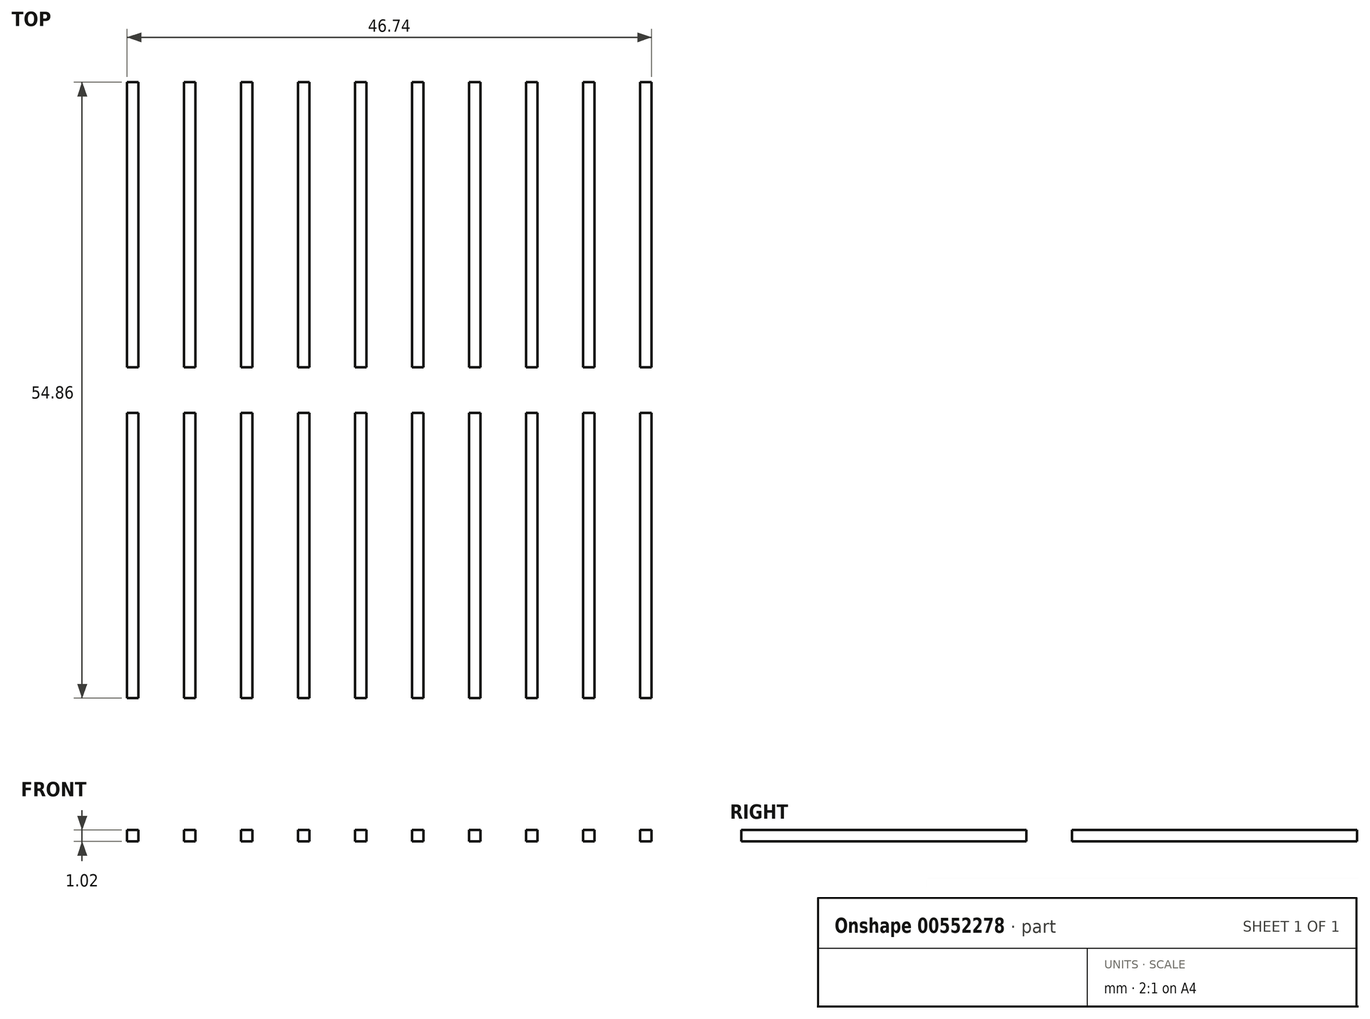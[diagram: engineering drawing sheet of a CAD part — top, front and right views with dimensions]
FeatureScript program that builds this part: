
annotation { "Feature Type Name" : "Feature", "Feature Type Description" : "" }
export const myFeature = defineFeature(function(context is Context, id is Id, definition is map)
    precondition{}
    {
        {
            var Q0;
            Q0=qCreatedBy(makeId("Top.planeOp"),FACE);
            var sketch = newSketch(context, id + "F0", { "sketchPlane" : qUnion([Q0])});
            skLineSegment(sketch, "E0.bottom", {"start": v(0, 0) * mm, "end": v(1.02, 0) * mm});
            skLineSegment(sketch, "E0.top", {"start": v(0, 25.4) * mm, "end": v(1.02, 25.4) * mm});
            skLineSegment(sketch, "E0.left", {"start": v(0, 0) * mm, "end": v(0, 25.4) * mm});
            skLineSegment(sketch, "E0.right", {"start": v(1.02, 0) * mm, "end": v(1.02, 25.4) * mm});
            skLineSegment(sketch, "E1.1.0.0", {"start": v(6.1, 0) * mm, "end": v(6.1, 25.4) * mm});
            skLineSegment(sketch, "E1.1.0.1", {"start": v(5.08, 0) * mm, "end": v(5.08, 25.4) * mm});
            skLineSegment(sketch, "E1.1.0.2", {"start": v(5.08, 25.4) * mm, "end": v(6.1, 25.4) * mm});
            skLineSegment(sketch, "E1.1.0.3", {"start": v(5.08, 0) * mm, "end": v(6.1, 0) * mm});
            skLineSegment(sketch, "E1.2.0.0", {"start": v(11.18, 0) * mm, "end": v(11.18, 25.4) * mm});
            skLineSegment(sketch, "E1.2.0.1", {"start": v(10.16, 0) * mm, "end": v(10.16, 25.4) * mm});
            skLineSegment(sketch, "E1.2.0.2", {"start": v(10.16, 25.4) * mm, "end": v(11.18, 25.4) * mm});
            skLineSegment(sketch, "E1.2.0.3", {"start": v(10.16, 0) * mm, "end": v(11.18, 0) * mm});
            skLineSegment(sketch, "E1.3.0.0", {"start": v(16.26, 0) * mm, "end": v(16.26, 25.4) * mm});
            skLineSegment(sketch, "E1.3.0.1", {"start": v(15.24, 0) * mm, "end": v(15.24, 25.4) * mm});
            skLineSegment(sketch, "E1.3.0.2", {"start": v(15.24, 25.4) * mm, "end": v(16.26, 25.4) * mm});
            skLineSegment(sketch, "E1.3.0.3", {"start": v(15.24, 0) * mm, "end": v(16.26, 0) * mm});
            skLineSegment(sketch, "E1.4.0.0", {"start": v(21.34, 0) * mm, "end": v(21.34, 25.4) * mm});
            skLineSegment(sketch, "E1.4.0.1", {"start": v(20.32, 0) * mm, "end": v(20.32, 25.4) * mm});
            skLineSegment(sketch, "E1.4.0.2", {"start": v(20.32, 25.4) * mm, "end": v(21.34, 25.4) * mm});
            skLineSegment(sketch, "E1.4.0.3", {"start": v(20.32, 0) * mm, "end": v(21.34, 0) * mm});
            skLineSegment(sketch, "E1.5.0.0", {"start": v(26.42, 0) * mm, "end": v(26.42, 25.4) * mm});
            skLineSegment(sketch, "E1.5.0.1", {"start": v(25.4, 0) * mm, "end": v(25.4, 25.4) * mm});
            skLineSegment(sketch, "E1.5.0.2", {"start": v(25.4, 25.4) * mm, "end": v(26.42, 25.4) * mm});
            skLineSegment(sketch, "E1.5.0.3", {"start": v(25.4, 0) * mm, "end": v(26.42, 0) * mm});
            skLineSegment(sketch, "E1.6.0.0", {"start": v(31.5, 0) * mm, "end": v(31.5, 25.4) * mm});
            skLineSegment(sketch, "E1.6.0.1", {"start": v(30.48, 0) * mm, "end": v(30.48, 25.4) * mm});
            skLineSegment(sketch, "E1.6.0.2", {"start": v(30.48, 25.4) * mm, "end": v(31.5, 25.4) * mm});
            skLineSegment(sketch, "E1.6.0.3", {"start": v(30.48, 0) * mm, "end": v(31.5, 0) * mm});
            skLineSegment(sketch, "E1.7.0.0", {"start": v(36.58, 0) * mm, "end": v(36.58, 25.4) * mm});
            skLineSegment(sketch, "E1.7.0.1", {"start": v(35.56, 0) * mm, "end": v(35.56, 25.4) * mm});
            skLineSegment(sketch, "E1.7.0.2", {"start": v(35.56, 25.4) * mm, "end": v(36.58, 25.4) * mm});
            skLineSegment(sketch, "E1.7.0.3", {"start": v(35.56, 0) * mm, "end": v(36.58, 0) * mm});
            skLineSegment(sketch, "E1.8.0.0", {"start": v(41.66, 0) * mm, "end": v(41.66, 25.4) * mm});
            skLineSegment(sketch, "E1.8.0.1", {"start": v(40.64, 0) * mm, "end": v(40.64, 25.4) * mm});
            skLineSegment(sketch, "E1.8.0.2", {"start": v(40.64, 25.4) * mm, "end": v(41.66, 25.4) * mm});
            skLineSegment(sketch, "E1.8.0.3", {"start": v(40.64, 0) * mm, "end": v(41.66, 0) * mm});
            skLineSegment(sketch, "E1.9.0.0", {"start": v(46.74, 0) * mm, "end": v(46.74, 25.4) * mm});
            skLineSegment(sketch, "E1.9.0.1", {"start": v(45.72, 0) * mm, "end": v(45.72, 25.4) * mm});
            skLineSegment(sketch, "E1.9.0.2", {"start": v(45.72, 25.4) * mm, "end": v(46.74, 25.4) * mm});
            skLineSegment(sketch, "E1.9.0.3", {"start": v(45.72, 0) * mm, "end": v(46.74, 0) * mm});
            skLineSegment(sketch, "E1.direction1", {"start": v(0, 0) * mm, "end": v(5.08, 0) * mm, "construction": true});
            skLineSegment(sketch, "E2.0.1.0", {"start": v(0, 29.46) * mm, "end": v(0, 54.86) * mm});
            skLineSegment(sketch, "E2.0.1.1", {"start": v(10.16, 29.46) * mm, "end": v(10.16, 54.86) * mm});
            skLineSegment(sketch, "E2.0.1.2", {"start": v(25.4, 29.46) * mm, "end": v(25.4, 54.86) * mm});
            skLineSegment(sketch, "E2.0.1.3", {"start": v(40.64, 29.46) * mm, "end": v(40.64, 54.86) * mm});
            skLineSegment(sketch, "E2.0.1.4", {"start": v(36.58, 29.46) * mm, "end": v(36.58, 54.86) * mm});
            skLineSegment(sketch, "E2.0.1.5", {"start": v(35.56, 29.46) * mm, "end": v(35.56, 54.86) * mm});
            skLineSegment(sketch, "E2.0.1.6", {"start": v(46.74, 29.46) * mm, "end": v(46.74, 54.86) * mm});
            skLineSegment(sketch, "E2.0.1.7", {"start": v(16.26, 29.46) * mm, "end": v(16.26, 54.86) * mm});
            skLineSegment(sketch, "E2.0.1.8", {"start": v(30.48, 29.46) * mm, "end": v(30.48, 54.86) * mm});
            skLineSegment(sketch, "E2.0.1.9", {"start": v(15.24, 29.46) * mm, "end": v(15.24, 54.86) * mm});
            skLineSegment(sketch, "E2.0.1.10", {"start": v(45.72, 29.46) * mm, "end": v(45.72, 54.86) * mm});
            skLineSegment(sketch, "E2.0.1.11", {"start": v(0, 29.46) * mm, "end": v(5.08, 29.46) * mm, "construction": true});
            skLineSegment(sketch, "E2.0.1.12", {"start": v(21.34, 29.46) * mm, "end": v(21.34, 54.86) * mm});
            skLineSegment(sketch, "E2.0.1.13", {"start": v(1.02, 29.46) * mm, "end": v(1.02, 54.86) * mm});
            skLineSegment(sketch, "E2.0.1.14", {"start": v(31.5, 29.46) * mm, "end": v(31.5, 54.86) * mm});
            skLineSegment(sketch, "E2.0.1.15", {"start": v(41.66, 29.46) * mm, "end": v(41.66, 54.86) * mm});
            skLineSegment(sketch, "E2.0.1.16", {"start": v(6.1, 29.46) * mm, "end": v(6.1, 54.86) * mm});
            skLineSegment(sketch, "E2.0.1.17", {"start": v(5.08, 29.46) * mm, "end": v(5.08, 54.86) * mm});
            skLineSegment(sketch, "E2.0.1.18", {"start": v(11.18, 29.46) * mm, "end": v(11.18, 54.86) * mm});
            skLineSegment(sketch, "E2.0.1.19", {"start": v(20.32, 29.46) * mm, "end": v(20.32, 54.86) * mm});
            skLineSegment(sketch, "E2.0.1.20", {"start": v(26.42, 29.46) * mm, "end": v(26.42, 54.86) * mm});
            skLineSegment(sketch, "E2.0.1.21", {"start": v(15.24, 29.46) * mm, "end": v(16.26, 29.46) * mm});
            skLineSegment(sketch, "E2.0.1.22", {"start": v(30.48, 54.86) * mm, "end": v(31.5, 54.86) * mm});
            skLineSegment(sketch, "E2.0.1.23", {"start": v(20.32, 29.46) * mm, "end": v(21.34, 29.46) * mm});
            skLineSegment(sketch, "E2.0.1.24", {"start": v(40.64, 29.46) * mm, "end": v(41.66, 29.46) * mm});
            skLineSegment(sketch, "E2.0.1.25", {"start": v(15.24, 54.86) * mm, "end": v(16.26, 54.86) * mm});
            skLineSegment(sketch, "E2.0.1.26", {"start": v(30.48, 29.46) * mm, "end": v(31.5, 29.46) * mm});
            skLineSegment(sketch, "E2.0.1.27", {"start": v(20.32, 54.86) * mm, "end": v(21.34, 54.86) * mm});
            skLineSegment(sketch, "E2.0.1.28", {"start": v(40.64, 54.86) * mm, "end": v(41.66, 54.86) * mm});
            skLineSegment(sketch, "E2.0.1.29", {"start": v(25.4, 29.46) * mm, "end": v(26.42, 29.46) * mm});
            skLineSegment(sketch, "E2.0.1.30", {"start": v(5.08, 54.86) * mm, "end": v(6.1, 54.86) * mm});
            skLineSegment(sketch, "E2.0.1.31", {"start": v(45.72, 29.46) * mm, "end": v(46.74, 29.46) * mm});
            skLineSegment(sketch, "E2.0.1.32", {"start": v(35.56, 29.46) * mm, "end": v(36.58, 29.46) * mm});
            skLineSegment(sketch, "E2.0.1.33", {"start": v(35.56, 54.86) * mm, "end": v(36.58, 54.86) * mm});
            skLineSegment(sketch, "E2.0.1.34", {"start": v(10.16, 54.86) * mm, "end": v(11.18, 54.86) * mm});
            skLineSegment(sketch, "E2.0.1.35", {"start": v(25.4, 54.86) * mm, "end": v(26.42, 54.86) * mm});
            skLineSegment(sketch, "E2.0.1.36", {"start": v(0, 54.86) * mm, "end": v(1.02, 54.86) * mm});
            skLineSegment(sketch, "E2.0.1.37", {"start": v(10.16, 29.46) * mm, "end": v(11.18, 29.46) * mm});
            skLineSegment(sketch, "E2.0.1.38", {"start": v(45.72, 54.86) * mm, "end": v(46.74, 54.86) * mm});
            skLineSegment(sketch, "E2.0.1.39", {"start": v(5.08, 29.46) * mm, "end": v(6.1, 29.46) * mm});
            skLineSegment(sketch, "E2.0.1.40", {"start": v(0, 29.46) * mm, "end": v(1.02, 29.46) * mm});
            skLineSegment(sketch, "E2.direction1", {"start": v(0, 0) * mm, "end": v(25.4, 0) * mm, "construction": true});
            skLineSegment(sketch, "E2.direction2", {"start": v(0, 0) * mm, "end": v(0, 29.46) * mm, "construction": true});
            skSolve(sketch);
        }
        {
            var Q0;
            Q0 = qSketchRegion(id + "F0", true);
            extrude(context, id + "F1", {"entities" : qUnion([Q0]), "depth" : 1.02 * mm, "offsetDistance" : 25.4 * mm});
        }
    });
